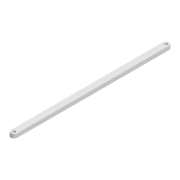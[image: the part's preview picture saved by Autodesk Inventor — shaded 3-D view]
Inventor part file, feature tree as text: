
AUTODESK INVENTOR PART (.ipt)
format: ipt  version: 2022 (Build 260153000, 153)  size: 86,016 bytes
history: native  units: mm
features: extrude x1, sketch x1
ambient origin geometry x8: Origin, YZ Plane, XZ Plane, XY Plane, X Axis, Y Axis, Z Axis, Center Point
bodies: Solid1 (feature_tree)
feature tree (2):
  extrude  "Extrusion1"  Depth=8.0mm
  sketch  "Sketch1"  dims[d0=190.0mm d1=8.0mm d2=4.2mm d3=4.2mm d4=5.0mm d5=0.0mm]
